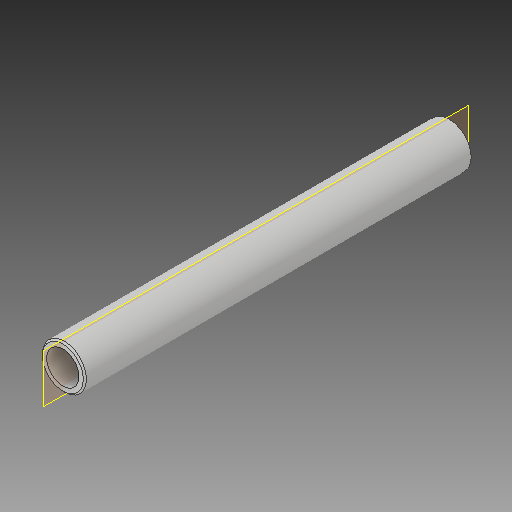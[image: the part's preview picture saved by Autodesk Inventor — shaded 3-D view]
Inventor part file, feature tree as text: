
AUTODESK INVENTOR PART (.ipt)
format: ipt  version: 2018 (Build 220112000, 112)  size: 90,112 bytes
history: native  units: mm
features: extrude x1, chamfer x1, sketch x1
ambient origin geometry x8: Origin, YZ Plane, XZ Plane, XY Plane, X Axis, Y Axis, Z Axis, Center Point
bodies: Solid1 (feature_tree)
feature tree (3):
  extrude  "Extrusion1"  Depth=500.72mm
  chamfer  "Chamfer1"  Distance=500.72mm
  sketch  "Sketch1"  dims[d0=57.2mm d1=41.9mm d2=500.72mm d3=0.0mm d4=2.0mm d5=2.0mm d6=45.0deg]
